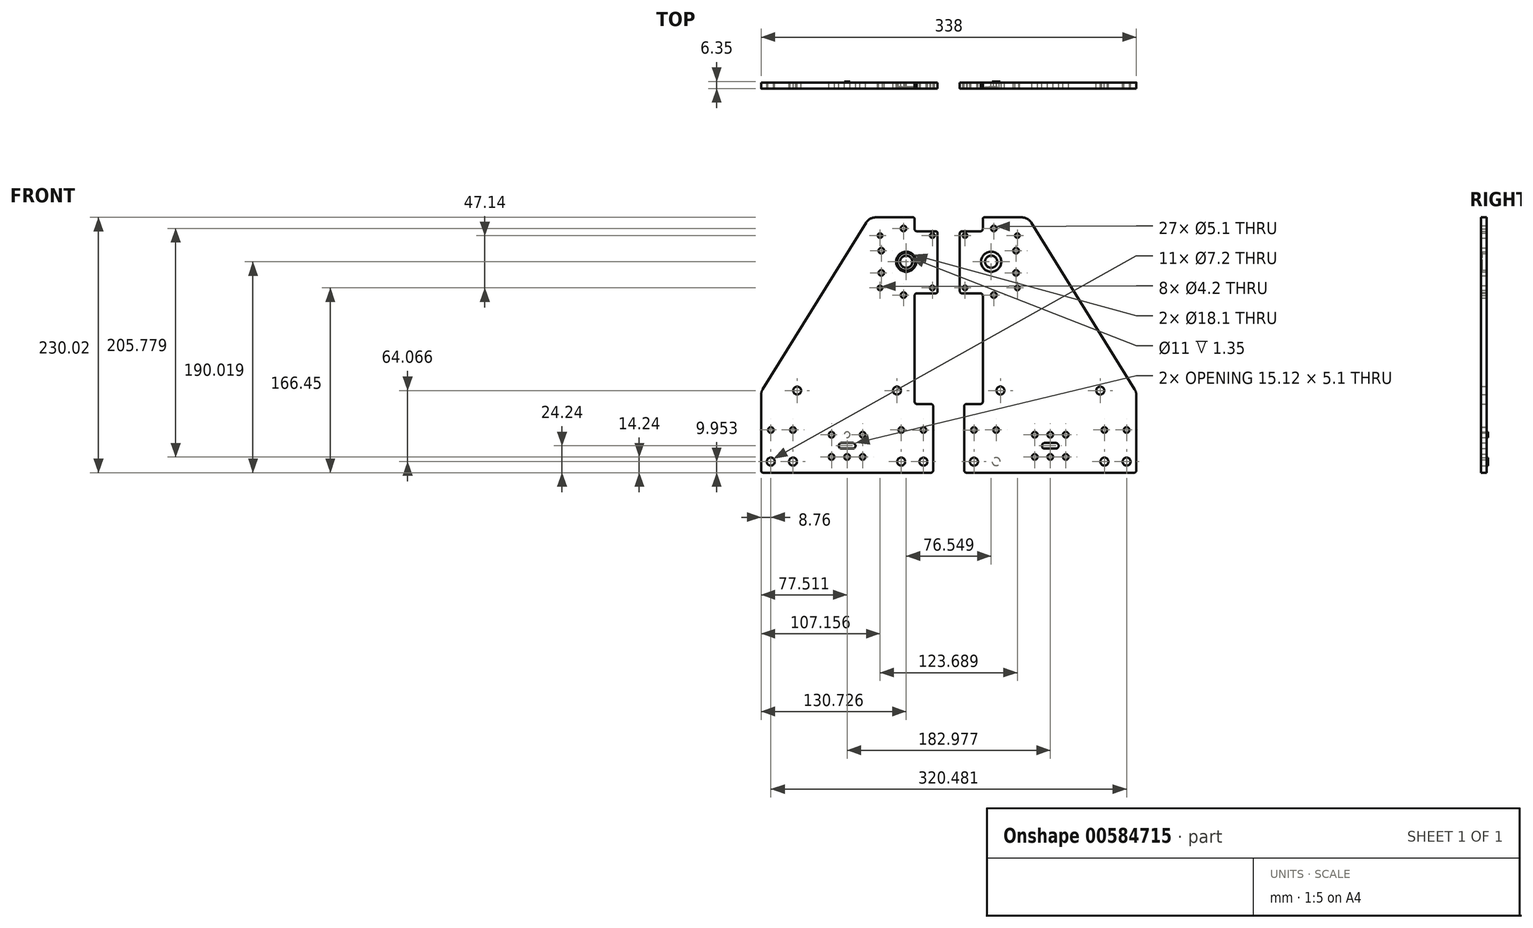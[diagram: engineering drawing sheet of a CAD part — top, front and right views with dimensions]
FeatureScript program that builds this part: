
annotation { "Feature Type Name" : "Feature", "Feature Type Description" : "" }
export const myFeature = defineFeature(function(context is Context, id is Id, definition is map)
    precondition{}
    {
        {
            var Q0;
            Q0=qCreatedBy(makeId("Front.planeOp"),FACE);
            var sketch = newSketch(context, id + "F0", { "sketchPlane" : qUnion([Q0])});
            skCircle(sketch, "E0", {"center": v(-38.27, 75) * mm, "radius": 9.05 * mm});
            skCircle(sketch, "E1", {"center": v(-91.5, -80.77) * mm, "radius": 2.55 * mm});
            skCircle(sketch, "E2", {"center": v(-91.5, -100.77) * mm, "radius": 2.55 * mm});
            skCircle(sketch, "E3", {"center": v(-105.5, -100.77) * mm, "radius": 2.55 * mm});
            skCircle(sketch, "E4", {"center": v(-105.5, -80.77) * mm, "radius": 2.55 * mm});
            skCircle(sketch, "E5", {"center": v(-77.5, -100.77) * mm, "radius": 2.55 * mm});
            skCircle(sketch, "E6", {"center": v(-77.5, -80.77) * mm, "radius": 2.55 * mm});
            skCircle(sketch, "E7", {"center": v(-40.67, 105) * mm, "radius": 2.55 * mm});
            skCircle(sketch, "E8", {"center": v(-40.67, 45) * mm, "radius": 2.55 * mm});
            skCircle(sketch, "E9", {"center": v(-60.67, 85) * mm, "radius": 2.55 * mm});
            skCircle(sketch, "E10", {"center": v(-60.67, 65) * mm, "radius": 2.55 * mm});
            skCircle(sketch, "E11", {"center": v(-61.84, 98.58) * mm, "radius": 2.1 * mm});
            skCircle(sketch, "E12", {"center": v(-61.84, 51.44) * mm, "radius": 2.1 * mm});
            skCircle(sketch, "E13", {"center": v(-14.7, 98.58) * mm, "radius": 2.1 * mm});
            skCircle(sketch, "E14", {"center": v(-14.7, 51.44) * mm, "radius": 2.1 * mm});
            skCircle(sketch, "E15", {"center": v(-160.24, -105) * mm, "radius": 3.6 * mm});
            skCircle(sketch, "E16", {"center": v(-140.24, -105) * mm, "radius": 3.6 * mm});
            skCircle(sketch, "E17", {"center": v(-160.24, -76.5) * mm, "radius": 2.55 * mm});
            skCircle(sketch, "E18", {"center": v(-140.24, -76.5) * mm, "radius": 2.55 * mm});
            skCircle(sketch, "E19", {"center": v(-136.5, -41) * mm, "radius": 3.6 * mm});
            skCircle(sketch, "E20", {"center": v(-22.76, -76.56) * mm, "radius": 2.55 * mm});
            skCircle(sketch, "E21", {"center": v(-42.76, -105) * mm, "radius": 3.6 * mm});
            skCircle(sketch, "E22", {"center": v(-46.6, -41) * mm, "radius": 3.6 * mm});
            skCircle(sketch, "E23", {"center": v(-42.76, -76.5) * mm, "radius": 2.55 * mm});
            skCircle(sketch, "E24", {"center": v(-22.76, -105.06) * mm, "radius": 3.6 * mm});
            skCircle(sketch, "E25", {"center": v(38.27, 75) * mm, "radius": 9.05 * mm});
            skCircle(sketch, "E26", {"center": v(38.27, 75) * mm, "radius": 5.5 * mm});
            skCircle(sketch, "E27", {"center": v(42.76, -105) * mm, "radius": 3.6 * mm});
            skCircle(sketch, "E28", {"center": v(136.5, -41) * mm, "radius": 3.6 * mm});
            skCircle(sketch, "E29", {"center": v(140.24, -76.5) * mm, "radius": 2.55 * mm});
            skCircle(sketch, "E30", {"center": v(160.24, -76.5) * mm, "radius": 2.55 * mm});
            skCircle(sketch, "E31", {"center": v(140.24, -105) * mm, "radius": 3.6 * mm});
            skCircle(sketch, "E32", {"center": v(160.24, -105) * mm, "radius": 3.6 * mm});
            skCircle(sketch, "E33", {"center": v(14.7, 51.44) * mm, "radius": 2.1 * mm});
            skCircle(sketch, "E34", {"center": v(14.7, 98.58) * mm, "radius": 2.1 * mm});
            skCircle(sketch, "E35", {"center": v(61.84, 51.44) * mm, "radius": 2.1 * mm});
            skCircle(sketch, "E36", {"center": v(61.84, 98.58) * mm, "radius": 2.1 * mm});
            skCircle(sketch, "E37", {"center": v(60.67, 65) * mm, "radius": 2.55 * mm});
            skCircle(sketch, "E38", {"center": v(40.67, 45) * mm, "radius": 2.55 * mm});
            skCircle(sketch, "E39", {"center": v(40.67, 105) * mm, "radius": 2.55 * mm});
            skCircle(sketch, "E40", {"center": v(77.5, -80.77) * mm, "radius": 2.55 * mm});
            skCircle(sketch, "E41", {"center": v(77.5, -100.77) * mm, "radius": 2.55 * mm});
            skCircle(sketch, "E42", {"center": v(105.5, -80.77) * mm, "radius": 2.55 * mm});
            skCircle(sketch, "E43", {"center": v(105.5, -100.77) * mm, "radius": 2.55 * mm});
            skCircle(sketch, "E44", {"center": v(91.5, -100.77) * mm, "radius": 2.55 * mm});
            skCircle(sketch, "E45", {"center": v(91.5, -80.77) * mm, "radius": 2.55 * mm});
            skCircle(sketch, "E46", {"center": v(60.67, 85) * mm, "radius": 2.55 * mm});
            skCircle(sketch, "E47", {"center": v(46.6, -41) * mm, "radius": 3.6 * mm});
            skCircle(sketch, "E48", {"center": v(22.76, -76.56) * mm, "radius": 2.55 * mm});
            skCircle(sketch, "E49", {"center": v(22.76, -105.06) * mm, "radius": 3.6 * mm});
            skCircle(sketch, "E50", {"center": v(42.76, -76.5) * mm, "radius": 2.55 * mm});
            skLineSegment(sketch, "E51", {"start": v(-86.48, -88.22) * mm, "end": v(-96.5, -88.22) * mm});
            skLineSegment(sketch, "E52", {"start": v(-96.5, -93.32) * mm, "end": v(-86.48, -93.32) * mm});
            skLineSegment(sketch, "E53", {"start": v(-30.68, 44.52) * mm, "end": v(-30.67, -51.13) * mm});
            skLineSegment(sketch, "E54", {"start": v(-12, 46.52) * mm, "end": v(-29, 46.52) * mm});
            skLineSegment(sketch, "E55", {"start": v(-10, 100.52) * mm, "end": v(-10, 48.52) * mm});
            skLineSegment(sketch, "E56", {"start": v(-29, 102.52) * mm, "end": v(-12, 102.52) * mm});
            skLineSegment(sketch, "E57", {"start": v(-30.67, 113.5) * mm, "end": v(-30.67, 104.52) * mm});
            skLineSegment(sketch, "E58", {"start": v(-65.81, 114.99) * mm, "end": v(-32.18, 115) * mm});
            skLineSegment(sketch, "E59", {"start": v(-167.5, -39.85) * mm, "end": v(-74.3, 110.26) * mm});
            skLineSegment(sketch, "E60", {"start": v(-169, -113) * mm, "end": v(-169, -45.12) * mm});
            skLineSegment(sketch, "E61", {"start": v(-16.3, -114.99) * mm, "end": v(-167, -115) * mm});
            skLineSegment(sketch, "E62", {"start": v(-14, -55.13) * mm, "end": v(-14, -113) * mm});
            skLineSegment(sketch, "E63", {"start": v(-28.67, -53.13) * mm, "end": v(-16, -53.13) * mm});
            skLineSegment(sketch, "E64", {"start": v(86.48, -88.22) * mm, "end": v(96.5, -88.22) * mm});
            skLineSegment(sketch, "E65", {"start": v(30.68, 44.52) * mm, "end": v(30.67, -51.13) * mm});
            skLineSegment(sketch, "E66", {"start": v(12, 46.52) * mm, "end": v(29, 46.52) * mm});
            skLineSegment(sketch, "E67", {"start": v(10, 100.52) * mm, "end": v(10, 48.52) * mm});
            skLineSegment(sketch, "E68", {"start": v(29, 102.52) * mm, "end": v(12, 102.52) * mm});
            skLineSegment(sketch, "E69", {"start": v(65.81, 114.99) * mm, "end": v(32.18, 115) * mm});
            skLineSegment(sketch, "E70", {"start": v(167.5, -39.85) * mm, "end": v(74.3, 110.26) * mm});
            skLineSegment(sketch, "E71", {"start": v(169, -113) * mm, "end": v(169, -45.12) * mm});
            skLineSegment(sketch, "E72", {"start": v(16.3, -114.99) * mm, "end": v(167, -115) * mm});
            skLineSegment(sketch, "E73", {"start": v(14, -55.13) * mm, "end": v(14, -113) * mm});
            skLineSegment(sketch, "E74", {"start": v(28.67, -53.13) * mm, "end": v(16, -53.13) * mm});
            skLineSegment(sketch, "E75", {"start": v(30.67, 113.5) * mm, "end": v(30.67, 104.52) * mm});
            skLineSegment(sketch, "E76", {"start": v(96.5, -93.32) * mm, "end": v(86.48, -93.32) * mm});
            skArc(sketch, "E77", {"start": v(-30.67, -51.13) * mm, "mid": v(-30.09, -52.54) * mm, "end": v(-28.67, -53.13) * mm});
            skArc(sketch, "E78", {"start": v(-86.48, -93.32) * mm, "mid": v(-83.93, -90.77) * mm, "end": v(-86.48, -88.22) * mm});
            skArc(sketch, "E79", {"start": v(-96.5, -88.22) * mm, "mid": v(-99.05, -90.77) * mm, "end": v(-96.5, -93.32) * mm});
            skArc(sketch, "E80", {"start": v(-29, 46.52) * mm, "mid": v(-30.21, 45.83) * mm, "end": v(-30.68, 44.52) * mm});
            skArc(sketch, "E81", {"start": v(-12, 46.52) * mm, "mid": v(-10.59, 47.1) * mm, "end": v(-10, 48.52) * mm});
            skArc(sketch, "E82", {"start": v(-10, 100.52) * mm, "mid": v(-10.59, 101.93) * mm, "end": v(-12, 102.52) * mm});
            skArc(sketch, "E83", {"start": v(-30.67, 104.52) * mm, "mid": v(-30.2, 103.2) * mm, "end": v(-29, 102.52) * mm});
            skArc(sketch, "E84", {"start": v(-30.67, 113.5) * mm, "mid": v(-31.11, 114.57) * mm, "end": v(-32.18, 115) * mm});
            skArc(sketch, "E85", {"start": v(-65.81, 114.99) * mm, "mid": v(-70.67, 113.73) * mm, "end": v(-74.3, 110.26) * mm});
            skArc(sketch, "E86", {"start": v(-167.5, -39.85) * mm, "mid": v(-168.62, -42.38) * mm, "end": v(-169, -45.12) * mm});
            skArc(sketch, "E87", {"start": v(-169, -113) * mm, "mid": v(-168.41, -114.42) * mm, "end": v(-167, -115) * mm});
            skArc(sketch, "E88", {"start": v(-16.3, -114.99) * mm, "mid": v(-14.7, -114.52) * mm, "end": v(-14, -113) * mm});
            skArc(sketch, "E89", {"start": v(-14, -55.13) * mm, "mid": v(-14.59, -53.71) * mm, "end": v(-16, -53.13) * mm});
            skArc(sketch, "E90", {"start": v(28.67, -53.13) * mm, "mid": v(30.09, -52.54) * mm, "end": v(30.67, -51.13) * mm});
            skArc(sketch, "E91", {"start": v(96.5, -93.32) * mm, "mid": v(99.05, -90.77) * mm, "end": v(96.5, -88.22) * mm});
            skArc(sketch, "E92", {"start": v(30.68, 44.52) * mm, "mid": v(30.21, 45.83) * mm, "end": v(29, 46.52) * mm});
            skArc(sketch, "E93", {"start": v(10, 48.52) * mm, "mid": v(10.59, 47.1) * mm, "end": v(12, 46.52) * mm});
            skArc(sketch, "E94", {"start": v(12, 102.52) * mm, "mid": v(10.59, 101.93) * mm, "end": v(10, 100.52) * mm});
            skArc(sketch, "E95", {"start": v(29, 102.52) * mm, "mid": v(30.2, 103.2) * mm, "end": v(30.67, 104.52) * mm});
            skArc(sketch, "E96", {"start": v(32.18, 115) * mm, "mid": v(31.11, 114.57) * mm, "end": v(30.67, 113.5) * mm});
            skArc(sketch, "E97", {"start": v(74.3, 110.26) * mm, "mid": v(70.67, 113.73) * mm, "end": v(65.81, 114.99) * mm});
            skArc(sketch, "E98", {"start": v(169, -45.12) * mm, "mid": v(168.62, -42.38) * mm, "end": v(167.5, -39.85) * mm});
            skArc(sketch, "E99", {"start": v(167, -115) * mm, "mid": v(168.41, -114.42) * mm, "end": v(169, -113) * mm});
            skArc(sketch, "E100", {"start": v(14, -113) * mm, "mid": v(14.7, -114.52) * mm, "end": v(16.3, -114.99) * mm});
            skArc(sketch, "E101", {"start": v(16, -53.13) * mm, "mid": v(14.59, -53.71) * mm, "end": v(14, -55.13) * mm});
            skArc(sketch, "E102", {"start": v(86.48, -88.22) * mm, "mid": v(83.93, -90.77) * mm, "end": v(86.48, -93.32) * mm});
            skCircle(sketch, "E103", {"center": v(-38.27, 75) * mm, "radius": 5.5 * mm});
            skCircle(sketch, "E104", {"center": v(-38.27, 75) * mm, "radius": 8.05 * mm});
            skCircle(sketch, "E105", {"center": v(38.27, 75) * mm, "radius": 8.05 * mm});
            skSolve(sketch);
        }
        {
            var Q0;
            Q0=makeQuery(id+"F0.imprint","IMPRINT",FACE,{"disambiguationData":[TD([[makeQuery(id+"F0.imprint","IMPRINT",EDGE,{"derivedFrom":sQuery(id+"F0.wireOp",EDGE,"E1")}),1.0]])]});
            var Q1;
            Q1=makeQuery(id+"F0.imprint","IMPRINT",FACE,{"disambiguationData":[TD([[makeQuery(id+"F0.imprint","IMPRINT",EDGE,{"derivedFrom":sQuery(id+"F0.wireOp",EDGE,"E103")}),-1.0]])]});
            var Q2;
            Q2=makeQuery(id+"F0.imprint","IMPRINT",FACE,{"disambiguationData":[TD([[makeQuery(id+"F0.imprint","IMPRINT",EDGE,{"derivedFrom":sQuery(id+"F0.wireOp",EDGE,"E0")}),-1.0]])]});
            extrude(context, id + "F1", {"entities" : qUnion([Q0, Q1, Q2]), "depth" : 6.35 * mm, "offsetDistance" : 25 * mm});
        }
        {
            var Q0;
            Q0=makeQuery(id+"F0.imprint","IMPRINT",FACE,{"disambiguationData":[TD([[makeQuery(id+"F0.imprint","IMPRINT",EDGE,{"derivedFrom":sQuery(id+"F0.wireOp",EDGE,"E103")}),-1.0]])]});
            var Q1;
            Q1=sQuery(id+"F0.wireOp",EDGE,"E104");
            var Q2;
            Q2=makeQuery(id+"F1.opExtrude","CAP_FACE",FACE,{"disambiguationData":[OSD([sQuery(id+"F0.wireOp",EDGE,"E1"),sQuery(id+"F0.wireOp",EDGE,"E2"),sQuery(id+"F0.wireOp",EDGE,"E3"),sQuery(id+"F0.wireOp",EDGE,"E4"),sQuery(id+"F0.wireOp",EDGE,"E5"),sQuery(id+"F0.wireOp",EDGE,"E6"),sQuery(id+"F0.wireOp",EDGE,"E7"),sQuery(id+"F0.wireOp",EDGE,"E8"),sQuery(id+"F0.wireOp",EDGE,"E9"),sQuery(id+"F0.wireOp",EDGE,"E10"),sQuery(id+"F0.wireOp",EDGE,"E11"),sQuery(id+"F0.wireOp",EDGE,"E12"),sQuery(id+"F0.wireOp",EDGE,"E13"),sQuery(id+"F0.wireOp",EDGE,"E14"),sQuery(id+"F0.wireOp",EDGE,"E15"),sQuery(id+"F0.wireOp",EDGE,"E16"),sQuery(id+"F0.wireOp",EDGE,"E17"),sQuery(id+"F0.wireOp",EDGE,"E18"),sQuery(id+"F0.wireOp",EDGE,"E19"),sQuery(id+"F0.wireOp",EDGE,"E20"),sQuery(id+"F0.wireOp",EDGE,"E21"),sQuery(id+"F0.wireOp",EDGE,"E22"),sQuery(id+"F0.wireOp",EDGE,"E23"),sQuery(id+"F0.wireOp",EDGE,"E24"),sQuery(id+"F0.wireOp",EDGE,"E51"),sQuery(id+"F0.wireOp",EDGE,"E52"),sQuery(id+"F0.wireOp",EDGE,"E53"),sQuery(id+"F0.wireOp",EDGE,"E54"),sQuery(id+"F0.wireOp",EDGE,"E55"),sQuery(id+"F0.wireOp",EDGE,"E56"),sQuery(id+"F0.wireOp",EDGE,"E57"),sQuery(id+"F0.wireOp",EDGE,"E58"),sQuery(id+"F0.wireOp",EDGE,"E59"),sQuery(id+"F0.wireOp",EDGE,"E60"),sQuery(id+"F0.wireOp",EDGE,"E61"),sQuery(id+"F0.wireOp",EDGE,"E62"),sQuery(id+"F0.wireOp",EDGE,"E63"),sQuery(id+"F0.wireOp",EDGE,"E77"),sQuery(id+"F0.wireOp",EDGE,"E78"),sQuery(id+"F0.wireOp",EDGE,"E79"),sQuery(id+"F0.wireOp",EDGE,"E80"),sQuery(id+"F0.wireOp",EDGE,"E81"),sQuery(id+"F0.wireOp",EDGE,"E82"),sQuery(id+"F0.wireOp",EDGE,"E83"),sQuery(id+"F0.wireOp",EDGE,"E84"),sQuery(id+"F0.wireOp",EDGE,"E85"),sQuery(id+"F0.wireOp",EDGE,"E86"),sQuery(id+"F0.wireOp",EDGE,"E87"),sQuery(id+"F0.wireOp",EDGE,"E88"),sQuery(id+"F0.wireOp",EDGE,"E89"),sQuery(id+"F0.wireOp",EDGE,"E103")])],"isStart":true});
            var Q3;
            Q3=makeQuery(id+"F2H0LuFetIU7Lti_1.opExtrude","SWEPT_BODY",BODY,{"disambiguationData":[OSD([sQuery(id+"F0.wireOp",EDGE,"E104")])]});
            extrude(context, id + "F2", {"entities" : qUnion([Q0]), "operationType" : NewBodyOperationType.REMOVE, "surfaceEntities" : qUnion([Q1]), "depth" : 5 * mm, "endBoundEntityFace" : qUnion([Q2]), "endBoundEntityBody" : qUnion([Q3]), "offsetDistance" : 5 * mm, "offsetOppositeDirection" : true});
        }
        {
            var Q0;
            Q0=makeQuery(id+"F0.imprint","IMPRINT",FACE,{"disambiguationData":[TD([[makeQuery(id+"F0.imprint","IMPRINT",EDGE,{"derivedFrom":sQuery(id+"F0.wireOp",EDGE,"E0")}),-1.0]])]});
            extrude(context, id + "F3", {"entities" : qUnion([Q0]), "operationType" : NewBodyOperationType.REMOVE, "depth" : 1 * mm, "offsetDistance" : 25 * mm});
        }
        {
            var Q0;
            Q0=makeQuery(id+"F0.imprint","IMPRINT",FACE,{"disambiguationData":[TD([[makeQuery(id+"F0.imprint","IMPRINT",EDGE,{"derivedFrom":sQuery(id+"F0.wireOp",EDGE,"E27")}),1.0]])]});
            var Q1;
            Q1=makeQuery(id+"F0.imprint","IMPRINT",FACE,{"disambiguationData":[TD([[makeQuery(id+"F0.imprint","IMPRINT",EDGE,{"derivedFrom":sQuery(id+"F0.wireOp",EDGE,"E25")}),-1.0]])]});
            var Q2;
            Q2=makeQuery(id+"F0.imprint","IMPRINT",FACE,{"disambiguationData":[TD([[makeQuery(id+"F0.imprint","IMPRINT",EDGE,{"derivedFrom":sQuery(id+"F0.wireOp",EDGE,"E26")}),1.0]])]});
            extrude(context, id + "F4", {"entities" : qUnion([Q0, Q1, Q2]), "depth" : 6.35 * mm, "offsetDistance" : 25 * mm});
        }
        {
            var Q0;
            Q0=makeQuery(id+"F0.imprint","IMPRINT",FACE,{"disambiguationData":[TD([[makeQuery(id+"F0.imprint","IMPRINT",EDGE,{"derivedFrom":sQuery(id+"F0.wireOp",EDGE,"E26")}),1.0]])]});
            extrude(context, id + "F5", {"entities" : qUnion([Q0]), "operationType" : NewBodyOperationType.REMOVE, "depth" : 5 * mm, "offsetDistance" : 25 * mm});
        }
        {
            var Q0;
            Q0=makeQuery(id+"F0.imprint","IMPRINT",FACE,{"disambiguationData":[TD([[makeQuery(id+"F0.imprint","IMPRINT",EDGE,{"derivedFrom":sQuery(id+"F0.wireOp",EDGE,"E25")}),-1.0]])]});
            extrude(context, id + "F6", {"entities" : qUnion([Q0]), "operationType" : NewBodyOperationType.REMOVE, "depth" : 1 * mm, "offsetDistance" : 25 * mm});
        }
    });
